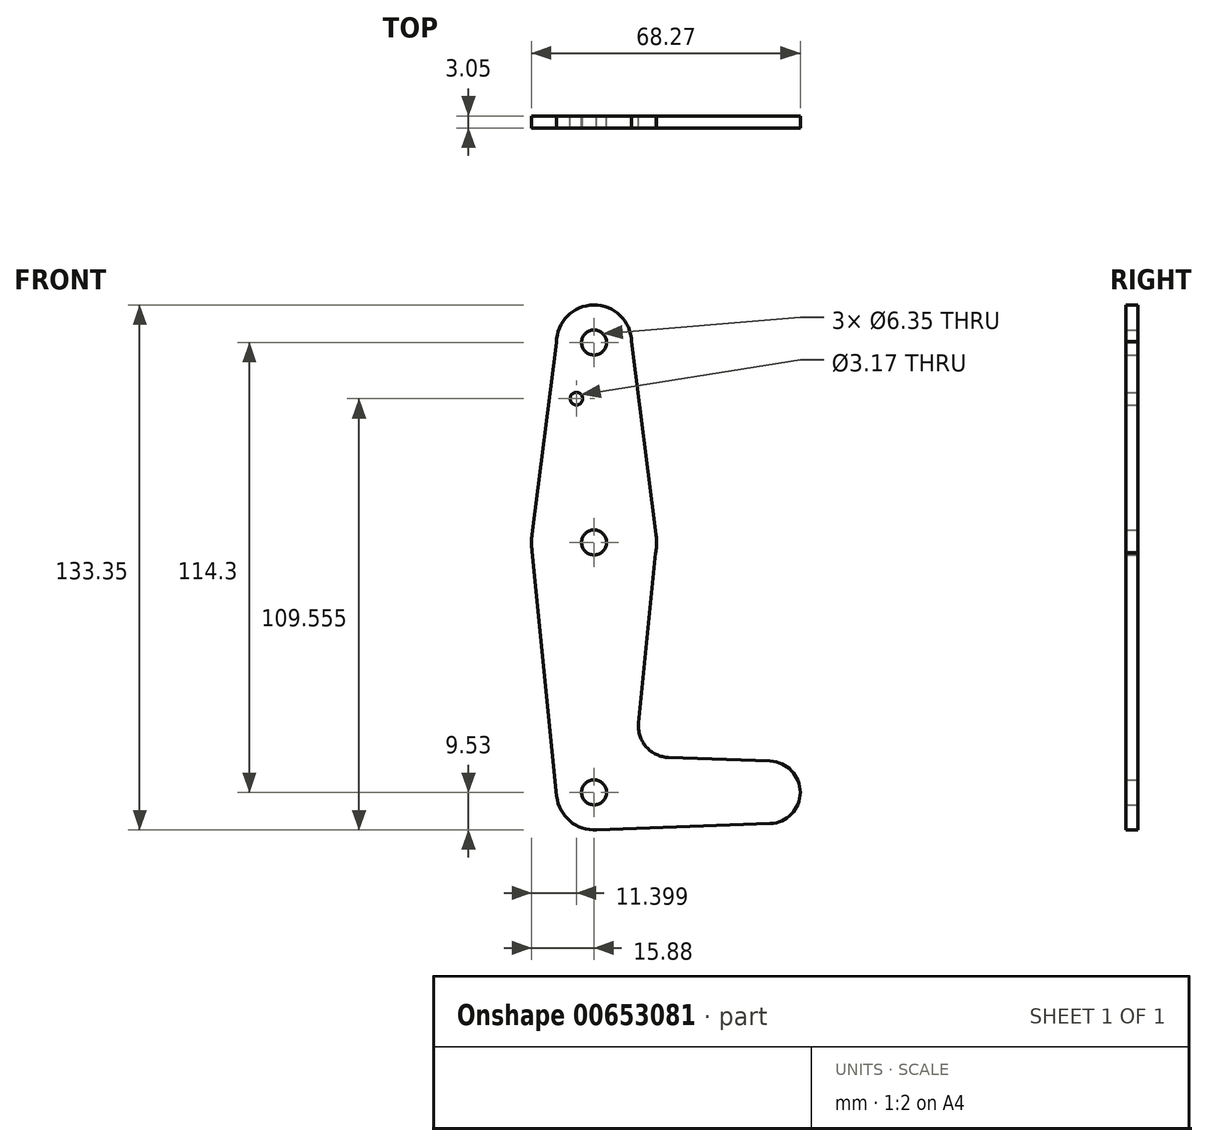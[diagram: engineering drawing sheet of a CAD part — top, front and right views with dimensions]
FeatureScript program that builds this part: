
annotation { "Feature Type Name" : "Feature", "Feature Type Description" : "" }
export const myFeature = defineFeature(function(context is Context, id is Id, definition is map)
    precondition{}
    {
        {
            var Q0;
            Q0=qCreatedBy(makeId("Front.planeOp"),FACE);
            var sketch = newSketch(context, id + "F0", { "sketchPlane" : qUnion([Q0])});
            skCircle(sketch, "E0", {"center": v(0, 0) * mm, "radius": 15.88 * mm});
            skCircle(sketch, "E1", {"center": v(0, 50.8) * mm, "radius": 9.53 * mm});
            skCircle(sketch, "E2", {"center": v(0, -63.5) * mm, "radius": 9.53 * mm});
            skLineSegment(sketch, "E3", {"start": v(0, -63.5) * mm, "end": v(44.45, -63.5) * mm});
            skCircle(sketch, "E4", {"center": v(44.45, -63.5) * mm, "radius": 7.94 * mm});
            skLineSegment(sketch, "E5", {"start": v(0, 50.8) * mm, "end": v(0, -63.5) * mm});
            skLineSegment(sketch, "E6", {"start": v(-9.52, 50.83) * mm, "end": v(-15.75, 2) * mm});
            skLineSegment(sketch, "E7", {"start": v(9.52, 51) * mm, "end": v(15.75, 2) * mm});
            skLineSegment(sketch, "E8", {"start": v(-15.7, -2.3) * mm, "end": v(-9.48, -64.45) * mm});
            skLineSegment(sketch, "E9", {"start": v(15.64, -2.7) * mm, "end": v(11.33, -45.91) * mm});
            skLineSegment(sketch, "E10", {"start": v(0, -73.03) * mm, "end": v(44.73, -71.43) * mm});
            skLineSegment(sketch, "E11", {"start": v(18.96, -54.65) * mm, "end": v(44.73, -55.57) * mm});
            skCircle(sketch, "E12", {"center": v(0, 50.8) * mm, "radius": 3.18 * mm});
            skCircle(sketch, "E13", {"center": v(-4.48, 36.53) * mm, "radius": 1.59 * mm});
            skArc(sketch, "E14.filletArc", {"start": v(11.33, -45.91) * mm, "mid": v(13.25, -51.93) * mm, "end": v(18.96, -54.65) * mm});
            skCircle(sketch, "E15", {"center": v(0, -63.5) * mm, "radius": 3.18 * mm});
            skCircle(sketch, "E16", {"center": v(0, 0) * mm, "radius": 3.17 * mm});
            skSolve(sketch);
        }
        {
            var Q0;
            Q0 = qSketchRegion(id + "F0", true);
            var Q1;
            {var subQ0=sQuery(id+"F0.wireOp",EDGE,"E5");var subQ1=sQuery(id+"F0.wireOp",EDGE,"E2");var subQ2=makeQuery(id+"F0.imprint","INTERSECT",VERTEX,{"derivedFrom":[subQ1,subQ0]});Q1=makeQuery(id+"F0.imprint","IMPRINT",FACE,{"disambiguationData":[TD([[makeQuery(id+"F0.imprint","IMPRINT",EDGE,{"disambiguationData":[TD([[subQ2,1.0]])],"derivedFrom":subQ1}),1.0]])]});}
            extrude(context, id + "F1", {"entities" : qUnion([Q0, Q1]), "depth" : 3.05 * mm, "offsetDistance" : 25.4 * mm});
        }
    });
